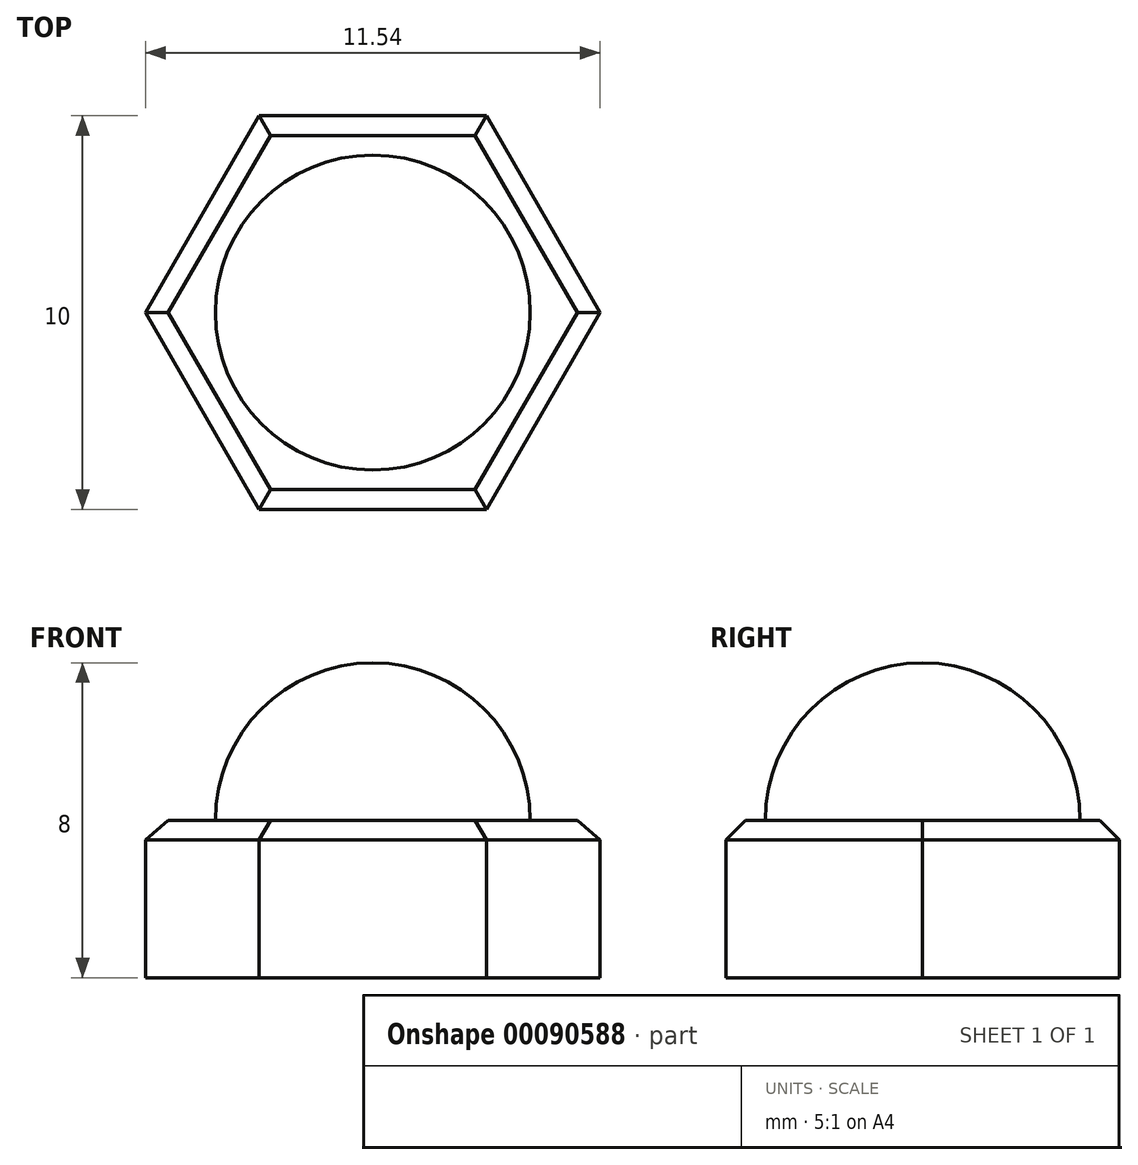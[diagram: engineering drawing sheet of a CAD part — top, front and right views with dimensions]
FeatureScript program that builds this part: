
annotation { "Feature Type Name" : "Feature", "Feature Type Description" : "" }
export const myFeature = defineFeature(function(context is Context, id is Id, definition is map)
    precondition{}
    {
        {
            var Q0;
            Q0=qCreatedBy(makeId("Top.planeOp"),FACE);
            var sketch = newSketch(context, id + "F0", { "sketchPlane" : qUnion([Q0])});
            skCircle(sketch, "E0.cCircle", {"center": v(0, 0) * mm, "radius": 5 * mm, "construction": true});
            skLineSegment(sketch, "E0.0", {"start": v(-2.89, 5) * mm, "end": v(2.89, 5) * mm});
            skLineSegment(sketch, "E0.1", {"start": v(2.89, 5) * mm, "end": v(5.77, 0) * mm});
            skLineSegment(sketch, "E0.2", {"start": v(5.77, 0) * mm, "end": v(2.89, -5) * mm});
            skLineSegment(sketch, "E0.3", {"start": v(2.89, -5) * mm, "end": v(-2.89, -5) * mm});
            skLineSegment(sketch, "E0.4", {"start": v(-2.89, -5) * mm, "end": v(-5.77, 0) * mm});
            skLineSegment(sketch, "E0.5", {"start": v(-5.77, 0) * mm, "end": v(-2.89, 5) * mm});
            skPoint(sketch, "E0.0.midPoint", {"position": v(0, 5) * mm});
            skSolve(sketch);
        }
        {
            var Q0;
            Q0=makeQuery(id+"F0.imprint","IMPRINT",FACE,{"disambiguationData":[TD([[makeQuery(id+"F0.imprint","IMPRINT",EDGE,{"derivedFrom":sQuery(id+"F0.wireOp",EDGE,"E0.0")}),-1.0]])]});
            extrude(context, id + "F1", {"entities" : qUnion([Q0]), "depth" : 4 * mm});
        }
        {
            var Q0;
            Q0=makeQuery(id+"F1.opExtrude","CAP_EDGE",EDGE,{"disambiguationData":[OSD([sQuery(id+"F0.wireOp",EDGE,"E0.2")])],"isStart":false});
            var Q1;
            Q1=makeQuery(id+"F1.opExtrude","CAP_EDGE",EDGE,{"disambiguationData":[OSD([sQuery(id+"F0.wireOp",EDGE,"E0.3")])],"isStart":false});
            var Q2;
            Q2=makeQuery(id+"F1.opExtrude","CAP_EDGE",EDGE,{"disambiguationData":[OSD([sQuery(id+"F0.wireOp",EDGE,"E0.4")])],"isStart":false});
            var Q3;
            Q3=makeQuery(id+"F1.opExtrude","CAP_EDGE",EDGE,{"disambiguationData":[OSD([sQuery(id+"F0.wireOp",EDGE,"E0.5")])],"isStart":false});
            var Q4;
            Q4=makeQuery(id+"F1.opExtrude","CAP_EDGE",EDGE,{"disambiguationData":[OSD([sQuery(id+"F0.wireOp",EDGE,"E0.0")])],"isStart":false});
            var Q5;
            Q5=makeQuery(id+"F1.opExtrude","CAP_EDGE",EDGE,{"disambiguationData":[OSD([sQuery(id+"F0.wireOp",EDGE,"E0.1")])],"isStart":false});
            chamfer(context, id + "F2", {"entities" : qUnion([Q0, Q1, Q2, Q3, Q4, Q5]), "width" : 0.5 * mm, "tangentPropagation" : true});
        }
        {
            var Q0;
            Q0=makeQuery(id+"F1.opExtrude","CAP_FACE",FACE,{"disambiguationData":[OSD([sQuery(id+"F0.wireOp",EDGE,"E0.0"),sQuery(id+"F0.wireOp",EDGE,"E0.1"),sQuery(id+"F0.wireOp",EDGE,"E0.2"),sQuery(id+"F0.wireOp",EDGE,"E0.3"),sQuery(id+"F0.wireOp",EDGE,"E0.4"),sQuery(id+"F0.wireOp",EDGE,"E0.5")])],"isStart":false});
            var sketch = newSketch(context, id + "F3", { "sketchPlane" : qUnion([Q0])});
            skArc(sketch, "E1", {"start": v(0, -4) * mm, "mid": v(4, 0) * mm, "end": v(0, 4) * mm});
            skLineSegment(sketch, "E2", {"start": v(0, 4) * mm, "end": v(0, -4) * mm});
            skSolve(sketch);
        }
        {
            var Q0;
            Q0 = qSketchRegion(id + "F3", true);
            var Q1;
            Q1=sQuery(id+"F3.wireOp",EDGE,"E2");
            revolve(context, id + "F4", {"operationType" : NewBodyOperationType.ADD, "entities" : qUnion([Q0]), "axis" : qUnion([Q1]), "revolveType" : RevolveType.FULL});
        }
    });
